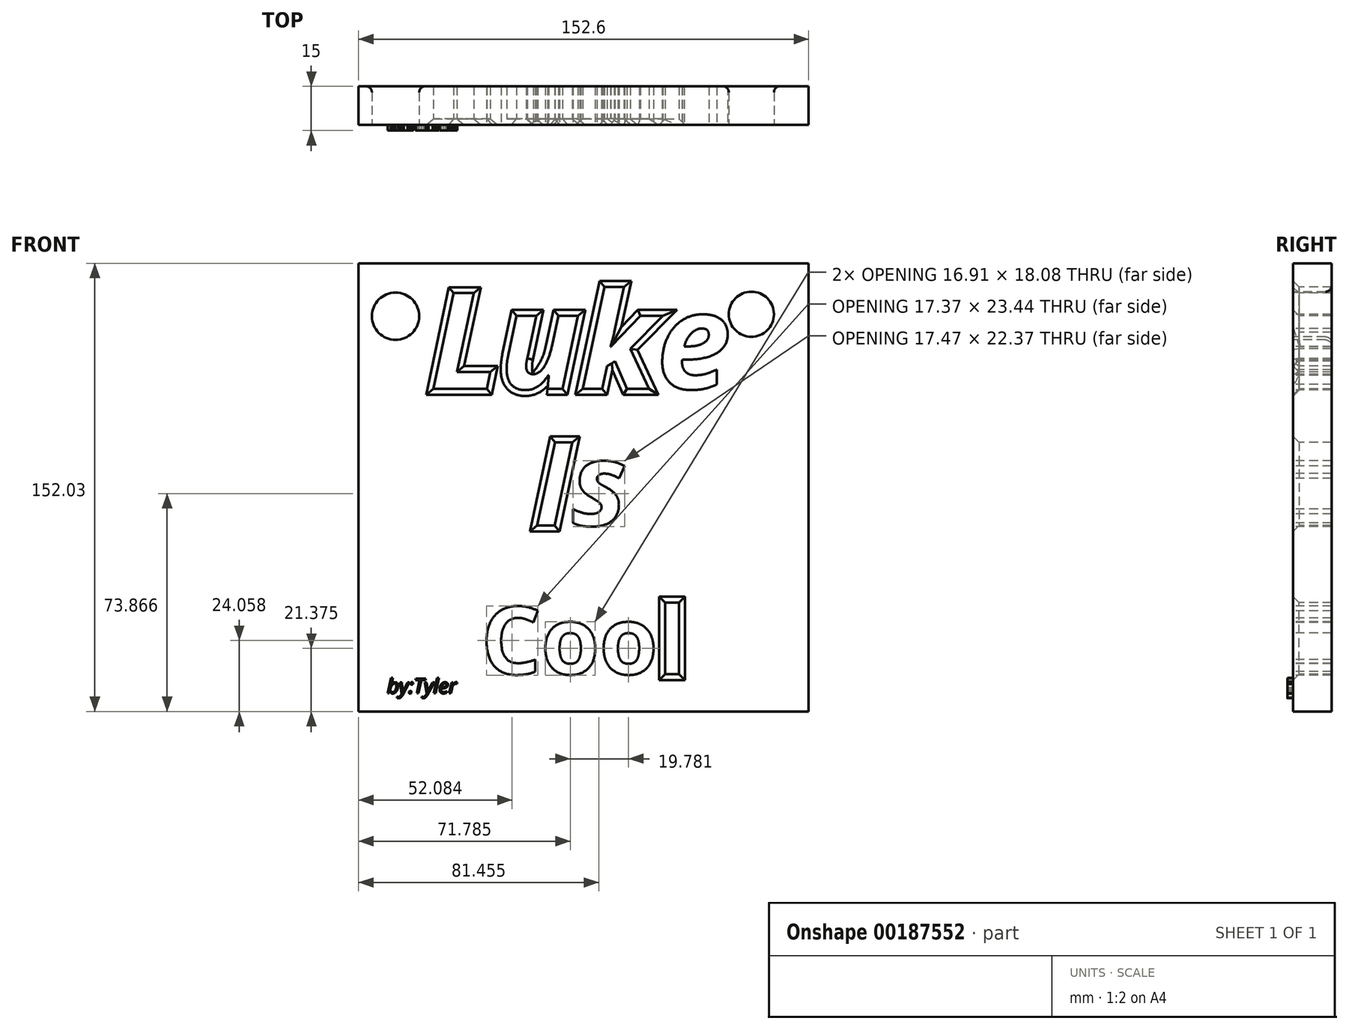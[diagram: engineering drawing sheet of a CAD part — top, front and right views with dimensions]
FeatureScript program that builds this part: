
annotation { "Feature Type Name" : "Feature", "Feature Type Description" : "" }
export const myFeature = defineFeature(function(context is Context, id is Id, definition is map)
    precondition{}
    {
        {
            var Q0;
            Q0=qCreatedBy(makeId("Front.planeOp"),FACE);
            var sketch = newSketch(context, id + "F0", { "sketchPlane" : qUnion([Q0])});
            skLineSegment(sketch, "E0.bottom", {"start": v(-76.16, 76.3) * mm, "end": v(76.44, 76.3) * mm});
            skLineSegment(sketch, "E0.top", {"start": v(-76.16, -75.73) * mm, "end": v(76.44, -75.73) * mm});
            skLineSegment(sketch, "E0.left", {"start": v(-76.16, 76.3) * mm, "end": v(-76.16, -75.73) * mm});
            skLineSegment(sketch, "E0.right", {"start": v(76.44, 76.3) * mm, "end": v(76.44, -75.73) * mm});
            skSolve(sketch);
        }
        {
            var Q0;
            Q0 = qSketchRegion(id + "F0", true);
            extrude(context, id + "F1", {"entities" : qUnion([Q0]), "depth" : 13 * mm});
        }
        {
            var Q0;
            Q0=makeQuery(id+"F1.opExtrude","CAP_FACE",FACE,{"disambiguationData":[OSD([sQuery(id+"F0.wireOp",EDGE,"E0.bottom"),sQuery(id+"F0.wireOp",EDGE,"E0.top"),sQuery(id+"F0.wireOp",EDGE,"E0.left"),sQuery(id+"F0.wireOp",EDGE,"E0.right")])],"isStart":false});
            var sketch = newSketch(context, id + "F2", { "sketchPlane" : qUnion([Q0])});
            skText(sketch, "E1", { "text": "Cool", "fontName": "OpenSans-Bold.ttf"});
            skText(sketch, "E2", { "text": "Luke", "fontName": "OpenSans-BoldItalic.ttf"});
            skText(sketch, "E3", { "text": "Is", "fontName": "OpenSans-BoldItalic.ttf"});
            const initialGuessF2  = {"E1": [-0.03462, -0.06308, 1, 0, 0.023], "E2": [-0.05197, 0.03372, 1, 0, 0.03272], "E3": [-0.0166, -0.01266, 1, 0, 0.02846]};
            skSetInitialGuess(sketch, initialGuessF2);
            skSolve(sketch);
        }
        {
            var Q0;
            Q0 = qSketchRegion(id + "F2", true);
            extrude(context, id + "F3", {"entities" : qUnion([Q0]), "operationType" : NewBodyOperationType.REMOVE, "oppositeDirection" : true, "depth" : 25 * mm});
        }
        {
            var Q0;
            {var subQ0=sQuery(id+"F0.wireOp",EDGE,"E0.left");var subQ1=sQuery(id+"F0.wireOp",EDGE,"E0.bottom");var subQ2=sQuery(id+"F0.wireOp",EDGE,"E0.right");var subQ3=sQuery(id+"F0.wireOp",EDGE,"E0.top");Q0=makeQuery(id+"F3.boolean.opBoolean","SPLIT",FACE,{"disambiguationData":[TD([makeQuery(id+"F1.opExtrude","SWEPT_FACE",FACE,{"disambiguationData":[OSD([subQ1])]})])],"derivedFrom":makeQuery(id+"F1.opExtrude","CAP_FACE",FACE,{"disambiguationData":[OSD([subQ1,subQ3,subQ0,subQ2])],"isStart":false})});}
            var sketch = newSketch(context, id + "F4", { "sketchPlane" : qUnion([Q0])});
            skCircle(sketch, "E4", {"center": v(-63.63, 58.33) * mm, "radius": 8.02 * mm});
            skCircle(sketch, "E5", {"center": v(57.05, 59) * mm, "radius": 7.65 * mm});
            skSolve(sketch);
        }
        {
            var Q0;
            Q0=makeQuery(id+"F4.imprint","IMPRINT",FACE,{"disambiguationData":[TD([[makeQuery(id+"F4.imprint","IMPRINT",EDGE,{"derivedFrom":sQuery(id+"F4.wireOp",EDGE,"E4")}),1.0]])]});
            var Q1;
            Q1=makeQuery(id+"F4.imprint","IMPRINT",FACE,{"disambiguationData":[TD([[makeQuery(id+"F4.imprint","IMPRINT",EDGE,{"derivedFrom":sQuery(id+"F4.wireOp",EDGE,"E5")}),1.0]])]});
            extrude(context, id + "F5", {"entities" : qUnion([Q0, Q1]), "operationType" : NewBodyOperationType.REMOVE, "oppositeDirection" : true, "depth" : 25 * mm});
        }
        {
            var Q0;
            {var subQ0=sQuery(id+"F0.wireOp",EDGE,"E0.left");var subQ1=sQuery(id+"F0.wireOp",EDGE,"E0.bottom");var subQ2=sQuery(id+"F0.wireOp",EDGE,"E0.right");var subQ3=sQuery(id+"F0.wireOp",EDGE,"E0.top");Q0=makeQuery(id+"F5.boolean.opBoolean","INTERSECT",EDGE,{"derivedFrom":[makeQuery(id+"F3.boolean.opBoolean","SPLIT",FACE,{"disambiguationData":[TD([makeQuery(id+"F1.opExtrude","SWEPT_FACE",FACE,{"disambiguationData":[OSD([subQ1])]})])],"derivedFrom":makeQuery(id+"F1.opExtrude","CAP_FACE",FACE,{"disambiguationData":[OSD([subQ1,subQ3,subQ0,subQ2])],"isStart":true})}),makeQuery(id+"F5.opExtrude","SWEPT_FACE",FACE,{"disambiguationData":[OSD([sQuery(id+"F4.wireOp",EDGE,"E4")])]})]});}
            var Q1;
            Q1=makeQuery(id+"F5.boolean.opBoolean","COPY",EDGE,{"derivedFrom":makeQuery(id+"F5.opExtrude","CAP_EDGE",EDGE,{"disambiguationData":[OSD([sQuery(id+"F4.wireOp",EDGE,"E4")])],"isStart":true})});
            var Q2;
            Q2=makeQuery(id+"F5.boolean.opBoolean","COPY",EDGE,{"derivedFrom":makeQuery(id+"F5.opExtrude","CAP_EDGE",EDGE,{"disambiguationData":[OSD([sQuery(id+"F4.wireOp",EDGE,"E5")])],"isStart":true})});
            var Q3;
            {var subQ0=sQuery(id+"F0.wireOp",EDGE,"E0.left");var subQ1=sQuery(id+"F0.wireOp",EDGE,"E0.bottom");var subQ2=sQuery(id+"F0.wireOp",EDGE,"E0.right");var subQ3=sQuery(id+"F0.wireOp",EDGE,"E0.top");Q3=makeQuery(id+"F5.boolean.opBoolean","INTERSECT",EDGE,{"derivedFrom":[makeQuery(id+"F3.boolean.opBoolean","SPLIT",FACE,{"disambiguationData":[TD([makeQuery(id+"F1.opExtrude","SWEPT_FACE",FACE,{"disambiguationData":[OSD([subQ1])]})])],"derivedFrom":makeQuery(id+"F1.opExtrude","CAP_FACE",FACE,{"disambiguationData":[OSD([subQ1,subQ3,subQ0,subQ2])],"isStart":true})}),makeQuery(id+"F5.opExtrude","SWEPT_FACE",FACE,{"disambiguationData":[OSD([sQuery(id+"F4.wireOp",EDGE,"E5")])]})]});}
            fillet(context, id + "F6", {"entities" : qUnion([Q0, Q1, Q2, Q3]), "radius" : 2 * mm, "tangentPropagation" : true, "allowEdgeOverflow" : false});
        }
        {
            var Q0;
            Q0=makeQuery(id+"F3.boolean.opBoolean","COPY",EDGE,{"derivedFrom":makeQuery(id+"F3.opExtrude","CAP_EDGE",EDGE,{"disambiguationData":[OSD([sQuery(id+"F2.wireOp",EDGE,"E2.sketch_text.stroke-0")])],"isStart":true})});
            var Q1;
            Q1=makeQuery(id+"F3.boolean.opBoolean","COPY",EDGE,{"derivedFrom":makeQuery(id+"F3.opExtrude","CAP_EDGE",EDGE,{"disambiguationData":[OSD([sQuery(id+"F2.wireOp",EDGE,"E2.sketch_text.stroke-1")])],"isStart":true})});
            var Q2;
            Q2=makeQuery(id+"F3.boolean.opBoolean","COPY",EDGE,{"derivedFrom":makeQuery(id+"F3.opExtrude","CAP_EDGE",EDGE,{"disambiguationData":[OSD([sQuery(id+"F2.wireOp",EDGE,"E2.sketch_text.stroke-2")])],"isStart":true})});
            var Q3;
            Q3=makeQuery(id+"F3.boolean.opBoolean","COPY",EDGE,{"derivedFrom":makeQuery(id+"F3.opExtrude","CAP_EDGE",EDGE,{"disambiguationData":[OSD([sQuery(id+"F2.wireOp",EDGE,"E2.sketch_text.stroke-3")])],"isStart":true})});
            var Q4;
            Q4=makeQuery(id+"F3.boolean.opBoolean","COPY",EDGE,{"derivedFrom":makeQuery(id+"F3.opExtrude","CAP_EDGE",EDGE,{"disambiguationData":[OSD([sQuery(id+"F2.wireOp",EDGE,"E2.sketch_text.stroke-4")])],"isStart":true})});
            var Q5;
            Q5=makeQuery(id+"F3.boolean.opBoolean","COPY",EDGE,{"derivedFrom":makeQuery(id+"F3.opExtrude","CAP_EDGE",EDGE,{"disambiguationData":[OSD([sQuery(id+"F2.wireOp",EDGE,"E2.sketch_text.stroke-5")])],"isStart":true})});
            var Q6;
            Q6=makeQuery(id+"F3.boolean.opBoolean","COPY",EDGE,{"derivedFrom":makeQuery(id+"F3.opExtrude","CAP_EDGE",EDGE,{"disambiguationData":[OSD([sQuery(id+"F2.wireOp",EDGE,"E2.sketch_text.stroke-22")])],"isStart":true})});
            var Q7;
            Q7=makeQuery(id+"F3.boolean.opBoolean","COPY",EDGE,{"derivedFrom":makeQuery(id+"F3.opExtrude","CAP_EDGE",EDGE,{"disambiguationData":[OSD([sQuery(id+"F2.wireOp",EDGE,"E2.sketch_text.stroke-21")])],"isStart":true})});
            var Q8;
            Q8=makeQuery(id+"F3.boolean.opBoolean","COPY",EDGE,{"derivedFrom":makeQuery(id+"F3.opExtrude","CAP_EDGE",EDGE,{"disambiguationData":[OSD([sQuery(id+"F2.wireOp",EDGE,"E2.sketch_text.stroke-7")])],"isStart":true})});
            var Q9;
            Q9=makeQuery(id+"F3.boolean.opBoolean","COPY",EDGE,{"derivedFrom":makeQuery(id+"F3.opExtrude","CAP_EDGE",EDGE,{"disambiguationData":[OSD([sQuery(id+"F2.wireOp",EDGE,"E2.sketch_text.stroke-6")])],"isStart":true})});
            var Q10;
            Q10=makeQuery(id+"F3.boolean.opBoolean","COPY",EDGE,{"derivedFrom":makeQuery(id+"F3.opExtrude","CAP_EDGE",EDGE,{"disambiguationData":[OSD([sQuery(id+"F2.wireOp",EDGE,"E2.sketch_text.stroke-12")])],"isStart":true})});
            var Q11;
            Q11=makeQuery(id+"F3.boolean.opBoolean","COPY",EDGE,{"derivedFrom":makeQuery(id+"F3.opExtrude","CAP_EDGE",EDGE,{"disambiguationData":[OSD([sQuery(id+"F2.wireOp",EDGE,"E2.sketch_text.stroke-13")])],"isStart":true})});
            var Q12;
            Q12=makeQuery(id+"F3.boolean.opBoolean","COPY",EDGE,{"derivedFrom":makeQuery(id+"F3.opExtrude","CAP_EDGE",EDGE,{"disambiguationData":[OSD([sQuery(id+"F2.wireOp",EDGE,"E2.sketch_text.stroke-14")])],"isStart":true})});
            var Q13;
            Q13=makeQuery(id+"F3.boolean.opBoolean","COPY",EDGE,{"derivedFrom":makeQuery(id+"F3.opExtrude","CAP_EDGE",EDGE,{"disambiguationData":[OSD([sQuery(id+"F2.wireOp",EDGE,"E2.sketch_text.stroke-15")])],"isStart":true})});
            var Q14;
            Q14=makeQuery(id+"F3.boolean.opBoolean","COPY",EDGE,{"derivedFrom":makeQuery(id+"F3.opExtrude","CAP_EDGE",EDGE,{"disambiguationData":[OSD([sQuery(id+"F2.wireOp",EDGE,"E2.sketch_text.stroke-31")])],"isStart":true})});
            var Q15;
            Q15=makeQuery(id+"F3.boolean.opBoolean","COPY",EDGE,{"derivedFrom":makeQuery(id+"F3.opExtrude","CAP_EDGE",EDGE,{"disambiguationData":[OSD([sQuery(id+"F2.wireOp",EDGE,"E2.sketch_text.stroke-33")])],"isStart":true})});
            var Q16;
            Q16=makeQuery(id+"F3.boolean.opBoolean","COPY",EDGE,{"derivedFrom":makeQuery(id+"F3.opExtrude","CAP_EDGE",EDGE,{"disambiguationData":[OSD([sQuery(id+"F2.wireOp",EDGE,"E2.sketch_text.stroke-32")])],"isStart":true})});
            var Q17;
            Q17=makeQuery(id+"F3.boolean.opBoolean","COPY",EDGE,{"derivedFrom":makeQuery(id+"F3.opExtrude","CAP_EDGE",EDGE,{"disambiguationData":[OSD([sQuery(id+"F2.wireOp",EDGE,"E2.sketch_text.stroke-23")])],"isStart":true})});
            var Q18;
            Q18=makeQuery(id+"F3.boolean.opBoolean","COPY",EDGE,{"derivedFrom":makeQuery(id+"F3.opExtrude","CAP_EDGE",EDGE,{"disambiguationData":[OSD([sQuery(id+"F2.wireOp",EDGE,"E2.sketch_text.stroke-30")])],"isStart":true})});
            var Q19;
            Q19=makeQuery(id+"F3.boolean.opBoolean","COPY",EDGE,{"derivedFrom":makeQuery(id+"F3.opExtrude","CAP_EDGE",EDGE,{"disambiguationData":[OSD([sQuery(id+"F2.wireOp",EDGE,"E2.sketch_text.stroke-27")])],"isStart":true})});
            var Q20;
            Q20=makeQuery(id+"F3.boolean.opBoolean","COPY",EDGE,{"derivedFrom":makeQuery(id+"F3.opExtrude","CAP_EDGE",EDGE,{"disambiguationData":[OSD([sQuery(id+"F2.wireOp",EDGE,"E2.sketch_text.stroke-29")])],"isStart":true})});
            var Q21;
            Q21=makeQuery(id+"F3.boolean.opBoolean","COPY",EDGE,{"derivedFrom":makeQuery(id+"F3.opExtrude","CAP_EDGE",EDGE,{"disambiguationData":[OSD([sQuery(id+"F2.wireOp",EDGE,"E2.sketch_text.stroke-37")])],"isStart":true})});
            var Q22;
            Q22=makeQuery(id+"F3.boolean.opBoolean","COPY",EDGE,{"derivedFrom":makeQuery(id+"F3.opExtrude","CAP_EDGE",EDGE,{"disambiguationData":[OSD([sQuery(id+"F2.wireOp",EDGE,"E2.sketch_text.stroke-26")])],"isStart":true})});
            var Q23;
            Q23=makeQuery(id+"F3.boolean.opBoolean","COPY",EDGE,{"derivedFrom":makeQuery(id+"F3.opExtrude","CAP_EDGE",EDGE,{"disambiguationData":[OSD([sQuery(id+"F2.wireOp",EDGE,"E2.sketch_text.stroke-25")])],"isStart":true})});
            var Q24;
            Q24=makeQuery(id+"F3.boolean.opBoolean","COPY",EDGE,{"derivedFrom":makeQuery(id+"F3.opExtrude","CAP_EDGE",EDGE,{"disambiguationData":[OSD([sQuery(id+"F2.wireOp",EDGE,"E2.sketch_text.stroke-24")])],"isStart":true})});
            var Q25;
            Q25=makeQuery(id+"F3.boolean.opBoolean","COPY",EDGE,{"derivedFrom":makeQuery(id+"F3.opExtrude","CAP_EDGE",EDGE,{"disambiguationData":[OSD([sQuery(id+"F2.wireOp",EDGE,"E3.sketch_text.stroke-0")])],"isStart":true})});
            var Q26;
            Q26=makeQuery(id+"F3.boolean.opBoolean","COPY",EDGE,{"derivedFrom":makeQuery(id+"F3.opExtrude","CAP_EDGE",EDGE,{"disambiguationData":[OSD([sQuery(id+"F2.wireOp",EDGE,"E3.sketch_text.stroke-1")])],"isStart":true})});
            var Q27;
            Q27=makeQuery(id+"F3.boolean.opBoolean","COPY",EDGE,{"derivedFrom":makeQuery(id+"F3.opExtrude","CAP_EDGE",EDGE,{"disambiguationData":[OSD([sQuery(id+"F2.wireOp",EDGE,"E3.sketch_text.stroke-2")])],"isStart":true})});
            var Q28;
            Q28=makeQuery(id+"F3.boolean.opBoolean","COPY",EDGE,{"derivedFrom":makeQuery(id+"F3.opExtrude","CAP_EDGE",EDGE,{"disambiguationData":[OSD([sQuery(id+"F2.wireOp",EDGE,"E3.sketch_text.stroke-3")])],"isStart":true})});
            var Q29;
            Q29=makeQuery(id+"F3.boolean.opBoolean","COPY",EDGE,{"derivedFrom":makeQuery(id+"F3.opExtrude","CAP_EDGE",EDGE,{"disambiguationData":[OSD([sQuery(id+"F2.wireOp",EDGE,"E1.sketch_text.stroke-52")])],"isStart":true})});
            var Q30;
            Q30=makeQuery(id+"F3.boolean.opBoolean","COPY",EDGE,{"derivedFrom":makeQuery(id+"F3.opExtrude","CAP_EDGE",EDGE,{"disambiguationData":[OSD([sQuery(id+"F2.wireOp",EDGE,"E1.sketch_text.stroke-53")])],"isStart":true})});
            var Q31;
            Q31=makeQuery(id+"F3.boolean.opBoolean","COPY",EDGE,{"derivedFrom":makeQuery(id+"F3.opExtrude","CAP_EDGE",EDGE,{"disambiguationData":[OSD([sQuery(id+"F2.wireOp",EDGE,"E1.sketch_text.stroke-54")])],"isStart":true})});
            var Q32;
            Q32=makeQuery(id+"F3.boolean.opBoolean","COPY",EDGE,{"derivedFrom":makeQuery(id+"F3.opExtrude","CAP_EDGE",EDGE,{"disambiguationData":[OSD([sQuery(id+"F2.wireOp",EDGE,"E1.sketch_text.stroke-51")])],"isStart":true})});
            chamfer(context, id + "F7", {"entities" : qUnion([Q0, Q1, Q2, Q3, Q4, Q5, Q6, Q7, Q8, Q9, Q10, Q11, Q12, Q13, Q14, Q15, Q16, Q17, Q18, Q19, Q20, Q21, Q22, Q23, Q24, Q25, Q26, Q27, Q28, Q29, Q30, Q31, Q32]), "width" : 2 * mm, "tangentPropagation" : true});
        }
        {
            var Q0;
            {var subQ0=sQuery(id+"F0.wireOp",EDGE,"E0.left");var subQ1=sQuery(id+"F0.wireOp",EDGE,"E0.bottom");var subQ2=sQuery(id+"F0.wireOp",EDGE,"E0.right");var subQ3=sQuery(id+"F0.wireOp",EDGE,"E0.top");Q0=makeQuery(id+"F3.boolean.opBoolean","SPLIT",FACE,{"disambiguationData":[TD([makeQuery(id+"F1.opExtrude","SWEPT_FACE",FACE,{"disambiguationData":[OSD([subQ1])]})])],"derivedFrom":makeQuery(id+"F1.opExtrude","CAP_FACE",FACE,{"disambiguationData":[OSD([subQ1,subQ3,subQ0,subQ2])],"isStart":false})});}
            var sketch = newSketch(context, id + "F8", { "sketchPlane" : qUnion([Q0])});
            skText(sketch, "E6", { "text": "by:Tyler", "fontName": "OpenSans-Italic.ttf"});
            const initialGuessF8  = {"E6": [-0.06645, -0.06958, 1, 0, 0.005]};
            skSetInitialGuess(sketch, initialGuessF8);
            skSolve(sketch);
        }
        {
            var Q0;
            Q0 = qSketchRegion(id + "F8", true);
            extrude(context, id + "F9", {"entities" : qUnion([Q0]), "operationType" : NewBodyOperationType.ADD, "depth" : 2 * mm});
        }
    });
